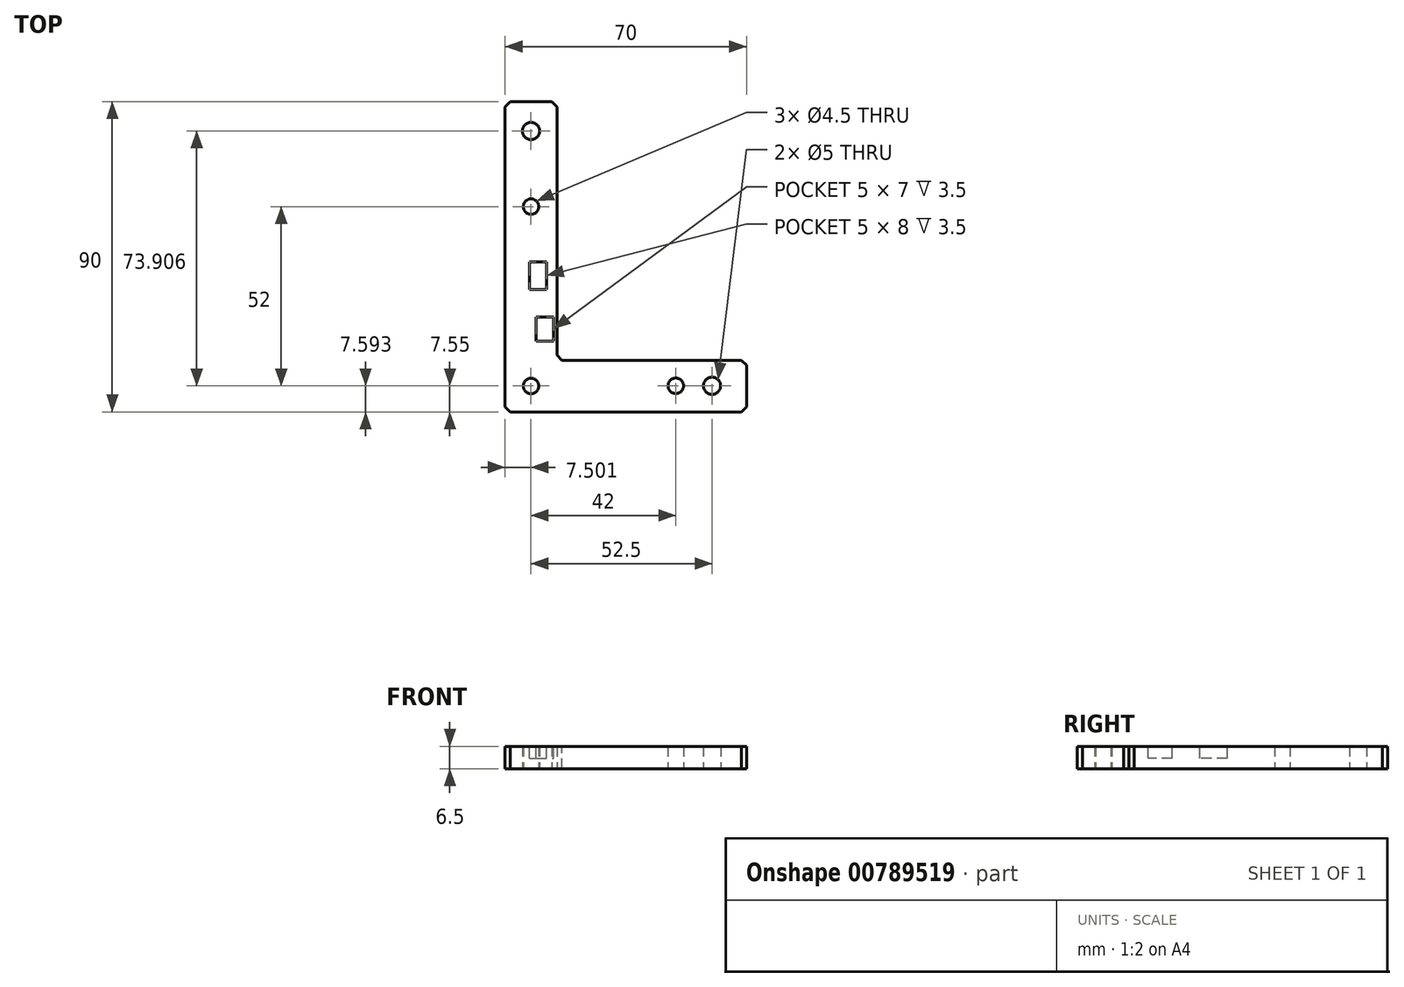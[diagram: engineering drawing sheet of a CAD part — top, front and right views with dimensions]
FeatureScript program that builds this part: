
annotation { "Feature Type Name" : "Feature", "Feature Type Description" : "" }
export const myFeature = defineFeature(function(context is Context, id is Id, definition is map)
    precondition{}
    {
        {
            var Q0;
            Q0=qCreatedBy(makeId("Top.planeOp"),FACE);
            var sketch = newSketch(context, id + "F0", { "sketchPlane" : qUnion([Q0])});
            skLineSegment(sketch, "E0", {"start": v(-36.85, 8.43) * mm, "end": v(-36.85, -81.57) * mm});
            skLineSegment(sketch, "E1", {"start": v(-36.85, -81.57) * mm, "end": v(33.15, -81.57) * mm});
            skLineSegment(sketch, "E2", {"start": v(33.15, -66.57) * mm, "end": v(-21.85, -66.57) * mm});
            skLineSegment(sketch, "E3", {"start": v(-21.85, -66.57) * mm, "end": v(-21.85, 8.43) * mm});
            skLineSegment(sketch, "E4.0", {"start": v(33.15, -66.37) * mm, "end": v(33.15, -66.57) * mm});
            skPoint(sketch, "E5.orphan", {"position": v(28.15, -66.57) * mm});
            skLineSegment(sketch, "E6", {"start": v(33.15, -66.37) * mm, "end": v(33.15, -81.57) * mm});
            skLineSegment(sketch, "E7", {"start": v(-36.85, 8.43) * mm, "end": v(-21.85, 8.43) * mm});
            skPoint(sketch, "E8.orphan", {"position": v(-36.85, -1.57) * mm});
            skPoint(sketch, "E9.start.orphan", {"position": v(-29.35, -1.57) * mm});
            skPoint(sketch, "E10.orphan", {"position": v(-21.85, -1.57) * mm});
            skPoint(sketch, "E11.end.orphan", {"position": v(28.15, -74.07) * mm});
            skPoint(sketch, "E11.start.orphan", {"position": v(28.15, -81.57) * mm});
            skCircle(sketch, "E12", {"center": v(-29.35, -74.02) * mm, "radius": 2.25 * mm});
            skCircle(sketch, "E13", {"center": v(12.65, -73.99) * mm, "radius": 2.25 * mm});
            skCircle(sketch, "E14", {"center": v(-29.35, -22.02) * mm, "radius": 2.25 * mm});
            skLineSegment(sketch, "E15.0", {"start": v(23.15, -66.37) * mm, "end": v(23.15, -66.57) * mm});
            skCircle(sketch, "E16", {"center": v(23.15, -73.98) * mm, "radius": 2.5 * mm});
            skCircle(sketch, "E17", {"center": v(-29.35, -0.07) * mm, "radius": 2.5 * mm});
            skPoint(sketch, "E18.orphan", {"position": v(-89.93, -74.07) * mm});
            skPoint(sketch, "E19.start.orphan", {"position": v(33.15, -73.97) * mm});
            skSolve(sketch);
        }
        {
            var Q0;
            Q0=makeQuery(id+"F0.imprint","IMPRINT",FACE,{"disambiguationData":[TD([[makeQuery(id+"F0.imprint","IMPRINT",EDGE,{"derivedFrom":sQuery(id+"F0.wireOp",EDGE,"E0")}),1.0]])]});
            extrude(context, id + "F1", {"entities" : qUnion([Q0]), "depth" : 6.5 * mm, "offsetDistance" : 25 * mm});
        }
        {
            var Q0;
            Q0=makeQuery(id+"F1.opExtrude","SWEPT_EDGE",EDGE,{"disambiguationData":[OSD([sQuery(id+"F0.wireOp",EDGE,"E3"),sQuery(id+"F0.wireOp",EDGE,"E7")])]});
            var Q1;
            Q1=makeQuery(id+"F1.opExtrude","SWEPT_EDGE",EDGE,{"disambiguationData":[OSD([sQuery(id+"F0.wireOp",EDGE,"E0"),sQuery(id+"F0.wireOp",EDGE,"E7")])]});
            var Q2;
            Q2=makeQuery(id+"F1.opExtrude","SWEPT_EDGE",EDGE,{"disambiguationData":[OSD([sQuery(id+"F0.wireOp",EDGE,"E0"),sQuery(id+"F0.wireOp",EDGE,"E1")])]});
            var Q3;
            Q3=makeQuery(id+"F1.opExtrude","SWEPT_EDGE",EDGE,{"disambiguationData":[OSD([sQuery(id+"F0.wireOp",EDGE,"E2"),sQuery(id+"F0.wireOp",EDGE,"E3")])]});
            var Q4;
            Q4=makeQuery(id+"F1.opExtrude","SWEPT_EDGE",EDGE,{"disambiguationData":[OSD([sQuery(id+"F0.wireOp",EDGE,"E2"),sQuery(id+"F0.wireOp",EDGE,"E6")])]});
            var Q5;
            Q5=makeQuery(id+"F1.opExtrude","SWEPT_EDGE",EDGE,{"disambiguationData":[OSD([sQuery(id+"F0.wireOp",EDGE,"E1"),sQuery(id+"F0.wireOp",EDGE,"E6")])]});
            chamfer(context, id + "F2", {"entities" : qUnion([Q0, Q1, Q2, Q3, Q4, Q5]), "width" : 1.5 * mm, "tangentPropagation" : true});
        }
        {
            var Q0;
            Q0=makeQuery(id+"F1.opExtrude","CAP_FACE",FACE,{"disambiguationData":[OSD([sQuery(id+"F0.wireOp",EDGE,"E0"),sQuery(id+"F0.wireOp",EDGE,"E1"),sQuery(id+"F0.wireOp",EDGE,"E2"),sQuery(id+"F0.wireOp",EDGE,"E3"),sQuery(id+"F0.wireOp",EDGE,"E6"),sQuery(id+"F0.wireOp",EDGE,"E7"),sQuery(id+"F0.wireOp",EDGE,"E12"),sQuery(id+"F0.wireOp",EDGE,"E13"),sQuery(id+"F0.wireOp",EDGE,"E14"),sQuery(id+"F0.wireOp",EDGE,"E16"),sQuery(id+"F0.wireOp",EDGE,"E17")])],"isStart":false});
            var sketch = newSketch(context, id + "F3", { "sketchPlane" : qUnion([Q0])});
            skLineSegment(sketch, "E20", {"start": v(-36.85, -38.02) * mm, "end": v(-36.85, -92.05) * mm, "construction": true});
            skLineSegment(sketch, "E21.bottom", {"start": v(-29.85, -38.02) * mm, "end": v(-24.85, -38.02) * mm});
            skLineSegment(sketch, "E21.top", {"start": v(-29.85, -46.02) * mm, "end": v(-24.85, -46.02) * mm});
            skLineSegment(sketch, "E21.left", {"start": v(-29.85, -38.02) * mm, "end": v(-29.85, -46.02) * mm});
            skLineSegment(sketch, "E21.right", {"start": v(-24.85, -38.02) * mm, "end": v(-24.85, -46.02) * mm});
            skLineSegment(sketch, "E22.bottom", {"start": v(-27.85, -54.02) * mm, "end": v(-22.85, -54.02) * mm});
            skLineSegment(sketch, "E22.top", {"start": v(-27.85, -61.02) * mm, "end": v(-22.85, -61.02) * mm});
            skLineSegment(sketch, "E22.left", {"start": v(-27.85, -54.02) * mm, "end": v(-27.85, -61.02) * mm});
            skLineSegment(sketch, "E22.right", {"start": v(-22.85, -54.02) * mm, "end": v(-22.85, -61.02) * mm});
            skSolve(sketch);
        }
        {
            var Q0;
            Q0 = qSketchRegion(id + "F3", true);
            extrude(context, id + "F4", {"entities" : qUnion([Q0]), "operationType" : NewBodyOperationType.REMOVE, "oppositeDirection" : true, "depth" : 3.5 * mm, "offsetDistance" : 25 * mm});
        }
    });
